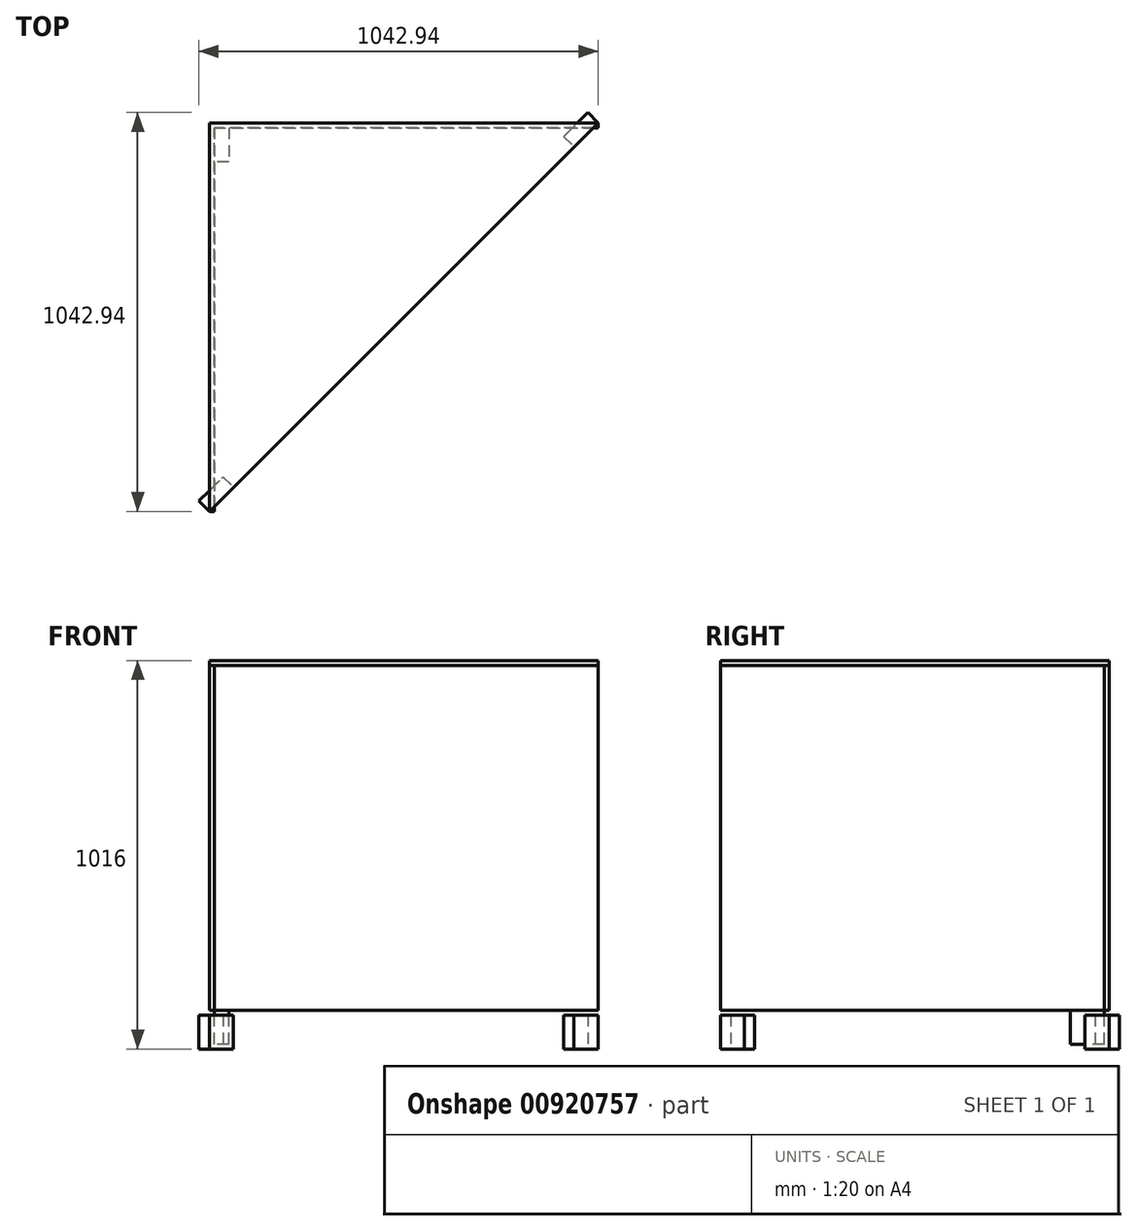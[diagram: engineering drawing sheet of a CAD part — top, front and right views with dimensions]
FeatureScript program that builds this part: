
annotation { "Feature Type Name" : "Feature", "Feature Type Description" : "" }
export const myFeature = defineFeature(function(context is Context, id is Id, definition is map)
    precondition{}
    {
        {
            var Q0;
            Q0=qCreatedBy(makeId("Top.planeOp"),FACE);
            var sketch = newSketch(context, id + "F0", { "sketchPlane" : qUnion([Q0])});
            skLineSegment(sketch, "E0", {"start": v(-1016, 453.25) * mm, "end": v(0, 453.25) * mm});
            skLineSegment(sketch, "E1", {"start": v(-1016, 453.25) * mm, "end": v(-1016, -562.75) * mm});
            skLineSegment(sketch, "E2", {"start": v(-1016, -562.75) * mm, "end": v(0, 453.25) * mm});
            skSolve(sketch);
        }
        {
            var Q0;
            Q0=sQuery(id+"F0.wireOp",EDGE,"E1");
            var Q1;
            Q1=sQuery(id+"F0.wireOp",EDGE,"E2");
            var Q2;
            Q2=sQuery(id+"F0.wireOp",EDGE,"E0");
            extrude(context, id + "F1", {"bodyType" : ToolBodyType.SURFACE, "surfaceEntities" : qUnion([Q0, Q1, Q2]), "depth" : 12.7 * mm, "offsetDistance" : 25 * mm});
        }
        {
            var Q0;
            Q0=makeQuery(id+"F1.opExtrude","SWEPT_FACE",FACE,{"disambiguationData":[OSD([sQuery(id+"F0.wireOp",EDGE,"E0")])]});
            var sketch = newSketch(context, id + "F2", { "sketchPlane" : qUnion([Q0])});
            skLineSegment(sketch, "E3.bottom", {"start": v(0, 12.7) * mm, "end": v(1016, 12.7) * mm});
            skLineSegment(sketch, "E3.top", {"start": v(0, 914.4) * mm, "end": v(1016, 914.4) * mm});
            skLineSegment(sketch, "E3.left", {"start": v(0, 12.7) * mm, "end": v(0, 914.4) * mm});
            skLineSegment(sketch, "E3.right", {"start": v(1016, 12.7) * mm, "end": v(1016, 914.4) * mm});
            skSolve(sketch);
        }
        {
            var Q0;
            Q0=makeQuery(id+"F2.imprint","IMPRINT",FACE,{"disambiguationData":[TD([[makeQuery(id+"F2.imprint","IMPRINT",EDGE,{"derivedFrom":sQuery(id+"F2.wireOp",EDGE,"E3.bottom")}),1.0]])]});
            extrude(context, id + "F3", {"entities" : qUnion([Q0]), "depth" : -12.7 * mm, "offsetDistance" : 25 * mm});
        }
        {
            var Q0;
            Q0=makeQuery(id+"F1.opExtrude","SWEPT_FACE",FACE,{"disambiguationData":[OSD([sQuery(id+"F0.wireOp",EDGE,"E1")])]});
            var sketch = newSketch(context, id + "F4", { "sketchPlane" : qUnion([Q0])});
            skLineSegment(sketch, "E4.bottom", {"start": v(-453.25, 12.7) * mm, "end": v(562.75, 12.7) * mm});
            skLineSegment(sketch, "E4.top", {"start": v(-453.25, 12.7) * mm, "end": v(562.75, 12.7) * mm});
            skLineSegment(sketch, "E4.left", {"start": v(-453.25, 12.7) * mm, "end": v(-453.25, 12.7) * mm});
            skLineSegment(sketch, "E4.right", {"start": v(562.75, 12.7) * mm, "end": v(562.75, 12.7) * mm});
            skLineSegment(sketch, "E5.bottom", {"start": v(562.75, 12.7) * mm, "end": v(-453.25, 12.7) * mm});
            skLineSegment(sketch, "E5.top", {"start": v(562.75, 914.4) * mm, "end": v(-453.25, 914.4) * mm});
            skLineSegment(sketch, "E5.left", {"start": v(562.75, 12.7) * mm, "end": v(562.75, 914.4) * mm});
            skLineSegment(sketch, "E5.right", {"start": v(-453.25, 12.7) * mm, "end": v(-453.25, 914.4) * mm});
            skSolve(sketch);
        }
        {
            var Q0;
            Q0 = qSketchRegion(id + "F4", true);
            extrude(context, id + "F5", {"entities" : qUnion([Q0]), "operationType" : NewBodyOperationType.ADD, "depth" : -12.7 * mm, "offsetDistance" : 25 * mm});
        }
        {
            var Q0;
            Q0=makeQuery(id+"F1.opExtrude","SWEPT_FACE",FACE,{"disambiguationData":[OSD([sQuery(id+"F0.wireOp",EDGE,"E2")])]});
            var sketch = newSketch(context, id + "F6", { "sketchPlane" : qUnion([Q0])});
            skLineSegment(sketch, "E6.bottom", {"start": v(-1116.35, 0) * mm, "end": v(-1027.45, 0) * mm});
            skLineSegment(sketch, "E6.top", {"start": v(-1116.35, -88.9) * mm, "end": v(-1027.45, -88.9) * mm});
            skLineSegment(sketch, "E6.left", {"start": v(-1116.35, 0) * mm, "end": v(-1116.35, -88.9) * mm});
            skLineSegment(sketch, "E6.right", {"start": v(-1027.45, 0) * mm, "end": v(-1027.45, -88.9) * mm});
            skLineSegment(sketch, "E7.bottom", {"start": v(320.5, 0) * mm, "end": v(231.6, 0) * mm});
            skLineSegment(sketch, "E7.top", {"start": v(320.5, -88.9) * mm, "end": v(231.6, -88.9) * mm});
            skLineSegment(sketch, "E7.left", {"start": v(320.5, 0) * mm, "end": v(320.5, -88.9) * mm});
            skLineSegment(sketch, "E7.right", {"start": v(231.6, 0) * mm, "end": v(231.6, -88.9) * mm});
            skSolve(sketch);
        }
        {
            var Q0;
            Q0 = qSketchRegion(id + "F6", true);
            extrude(context, id + "F7", {"entities" : qUnion([Q0]), "depth" : -38.1 * mm, "offsetDistance" : 25 * mm});
        }
        {
            var Q0;
            Q0=makeQuery(id+"F5.boolean.opBoolean","MERGE",FACE,{"derivedFrom":[makeQuery(id+"F3.opExtrude","SWEPT_FACE",FACE,{"disambiguationData":[OSD([sQuery(id+"F2.wireOp",EDGE,"E3.bottom")])]}),makeQuery(id+"F5.opExtrude","SWEPT_FACE",FACE,{"disambiguationData":[OSD([sQuery(id+"F4.wireOp",EDGE,"E5.bottom")])]})]});
            var sketch = newSketch(context, id + "F8", { "sketchPlane" : qUnion([Q0])});
            skLineSegment(sketch, "E8.bottom", {"start": v(-965.2, -440.55) * mm, "end": v(-1003.3, -440.55) * mm});
            skLineSegment(sketch, "E8.top", {"start": v(-965.2, -351.65) * mm, "end": v(-1003.3, -351.65) * mm});
            skLineSegment(sketch, "E8.left", {"start": v(-965.2, -440.55) * mm, "end": v(-965.2, -351.65) * mm});
            skLineSegment(sketch, "E8.right", {"start": v(-1003.3, -440.55) * mm, "end": v(-1003.3, -351.65) * mm});
            skSolve(sketch);
        }
        {
            var Q0;
            Q0 = qSketchRegion(id + "F8", true);
            extrude(context, id + "F9", {"entities" : qUnion([Q0]), "depth" : 88.9 * mm, "offsetDistance" : 25 * mm});
        }
        {
            var Q0;
            Q0=makeQuery(id+"F5.boolean.opBoolean","MERGE",FACE,{"derivedFrom":[makeQuery(id+"F3.opExtrude","SWEPT_FACE",FACE,{"disambiguationData":[OSD([sQuery(id+"F2.wireOp",EDGE,"E3.top")])]}),makeQuery(id+"F5.opExtrude","SWEPT_FACE",FACE,{"disambiguationData":[OSD([sQuery(id+"F4.wireOp",EDGE,"E5.top")])]})]});
            var sketch = newSketch(context, id + "F10", { "sketchPlane" : qUnion([Q0])});
            skLineSegment(sketch, "E9", {"start": v(-1016, -562.75) * mm, "end": v(0, 453.25) * mm});
            skLineSegment(sketch, "E10", {"start": v(0, 453.25) * mm, "end": v(-1016, 453.25) * mm});
            skLineSegment(sketch, "E11", {"start": v(-1016, -562.75) * mm, "end": v(-1016, 453.25) * mm});
            skSolve(sketch);
        }
        {
            var Q0;
            Q0 = qSketchRegion(id + "F10", true);
            extrude(context, id + "F11", {"entities" : qUnion([Q0]), "operationType" : NewBodyOperationType.ADD, "depth" : 12.7 * mm, "offsetDistance" : 25 * mm});
        }
    });
